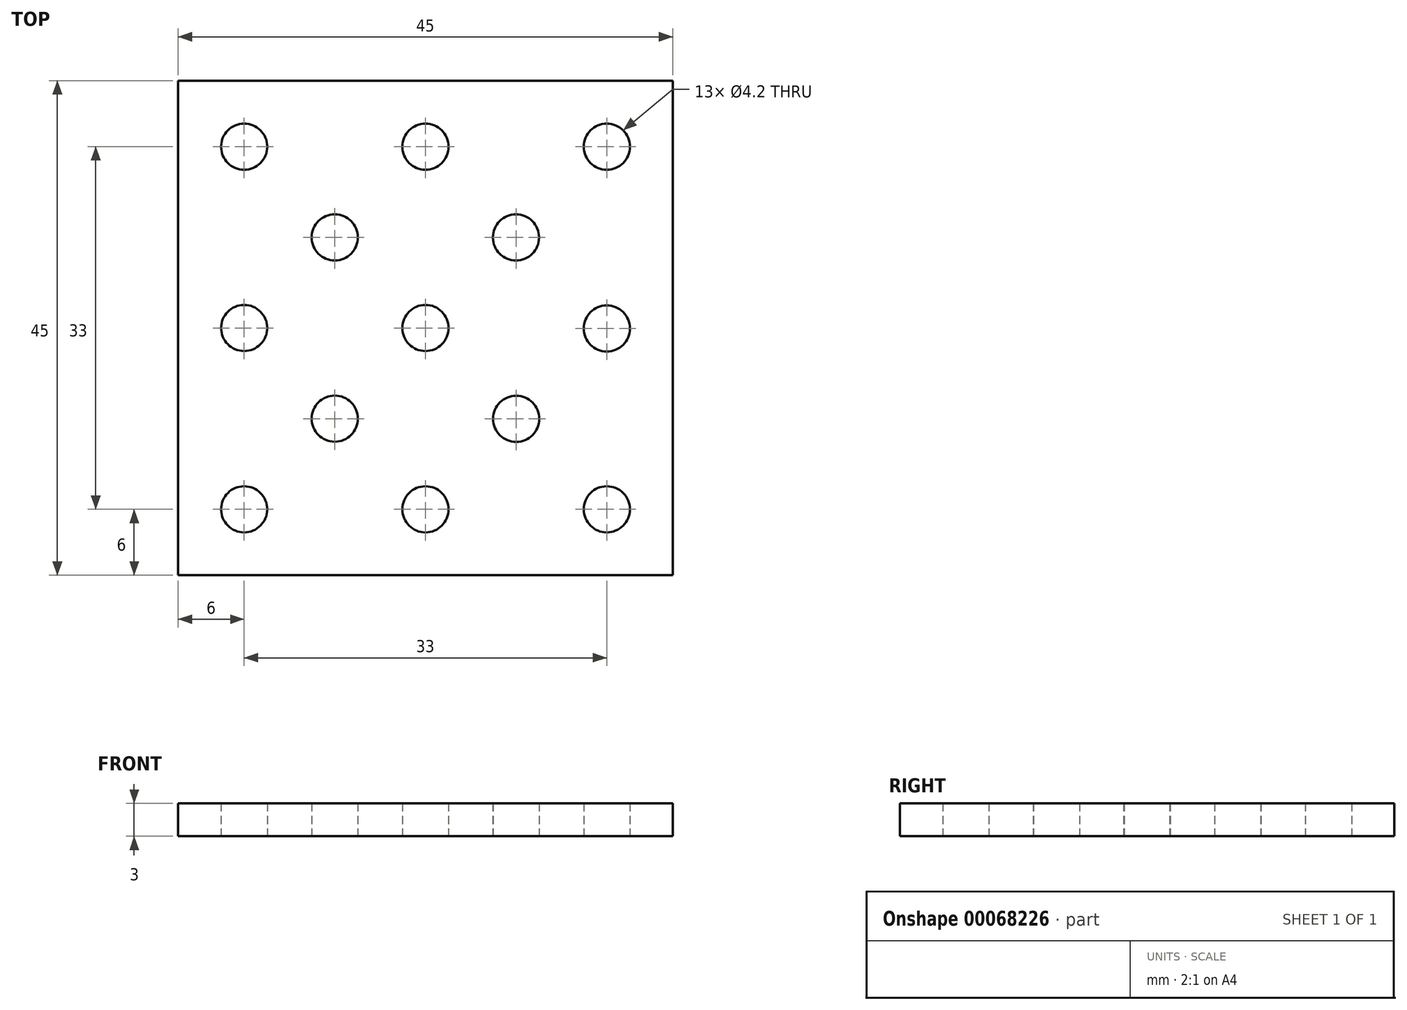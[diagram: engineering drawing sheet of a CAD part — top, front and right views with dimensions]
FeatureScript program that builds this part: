
annotation { "Feature Type Name" : "Feature", "Feature Type Description" : "" }
export const myFeature = defineFeature(function(context is Context, id is Id, definition is map)
    precondition{}
    {
        {
            var Q0;
            Q0=qCreatedBy(makeId("Top.planeOp"),FACE);
            var sketch = newSketch(context, id + "F0", { "sketchPlane" : qUnion([Q0])});
            skLineSegment(sketch, "E0.rect.bottom", {"start": v(-22.5, 22.5) * mm, "end": v(22.5, 22.5) * mm});
            skLineSegment(sketch, "E0.rect.top", {"start": v(-22.5, -22.5) * mm, "end": v(22.5, -22.5) * mm});
            skLineSegment(sketch, "E0.rect.left", {"start": v(-22.5, 22.5) * mm, "end": v(-22.5, -22.5) * mm});
            skLineSegment(sketch, "E0.rect.right", {"start": v(22.5, 22.5) * mm, "end": v(22.5, -22.5) * mm});
            skPoint(sketch, "E0.rect.middle", {"position": v(0, 0) * mm});
            skCircle(sketch, "E1", {"center": v(-16.5, 16.5) * mm, "radius": 2.1 * mm});
            skCircle(sketch, "E2.MirrorC", {"center": v(16.5, 16.5) * mm, "radius": 2.1 * mm});
            skCircle(sketch, "E3.MirrorC", {"center": v(16.5, -16.5) * mm, "radius": 2.1 * mm});
            skCircle(sketch, "E4.MirrorC", {"center": v(-16.5, -16.5) * mm, "radius": 2.1 * mm});
            skCircle(sketch, "E5.MirrorC", {"center": v(16.5, -0.05) * mm, "radius": 2.1 * mm});
            skLineSegment(sketch, "E6", {"start": v(16.5, 16.5) * mm, "end": v(16.5, -16.5) * mm, "construction": true});
            skLineSegment(sketch, "E7", {"start": v(16.5, -16.5) * mm, "end": v(-16.5, -16.5) * mm, "construction": true});
            skLineSegment(sketch, "E8", {"start": v(-16.5, -16.5) * mm, "end": v(-16.5, 16.5) * mm, "construction": true});
            skLineSegment(sketch, "E9", {"start": v(-16.5, 16.5) * mm, "end": v(16.5, 16.5) * mm, "construction": true});
            skCircle(sketch, "E10.MirrorC", {"center": v(0, -16.5) * mm, "radius": 2.1 * mm});
            skLineSegment(sketch, "E11", {"start": v(-16.5, 0) * mm, "end": v(0, -16.5) * mm, "construction": true});
            skLineSegment(sketch, "E12", {"start": v(16.5, -0.05) * mm, "end": v(0, -16.5) * mm, "construction": true});
            skLineSegment(sketch, "E13", {"start": v(16.5, -0.05) * mm, "end": v(0, 16.5) * mm, "construction": true});
            skLineSegment(sketch, "E14", {"start": v(-16.5, -16.5) * mm, "end": v(16.5, 16.5) * mm, "construction": true});
            skPoint(sketch, "E15", {"position": v(8.24, 8.24) * mm});
            skPoint(sketch, "E16", {"position": v(-8.25, -8.25) * mm});
            skCircle(sketch, "E17.MirrorC", {"center": v(-8.25, -8.25) * mm, "radius": 2.1 * mm});
            skCircle(sketch, "E18.MirrorC", {"center": v(8.24, 8.24) * mm, "radius": 2.1 * mm});
            skLineSegment(sketch, "E19", {"start": v(-16.5, 16.5) * mm, "end": v(16.5, -16.5) * mm, "construction": true});
            skPoint(sketch, "E20", {"position": v(8.26, -8.26) * mm});
            skCircle(sketch, "E21.MirrorC", {"center": v(8.26, -8.26) * mm, "radius": 2.1 * mm});
            skLineSegment(sketch, "E22.bottom", {"start": v(-22.5, 22.5) * mm, "end": v(7.5, 22.5) * mm, "construction": true});
            skLineSegment(sketch, "E22.top", {"start": v(-22.5, -7.5) * mm, "end": v(7.5, -7.5) * mm, "construction": true});
            skLineSegment(sketch, "E22.left", {"start": v(-22.5, 22.5) * mm, "end": v(-22.5, -7.5) * mm, "construction": true});
            skLineSegment(sketch, "E22.right", {"start": v(7.5, 22.5) * mm, "end": v(7.5, -7.5) * mm, "construction": true});
            skCircle(sketch, "E23.MirrorC", {"center": v(0, 0) * mm, "radius": 2.1 * mm});
            skPoint(sketch, "E24", {"position": v(-16.5, 0) * mm});
            skCircle(sketch, "E25.MirrorC", {"center": v(-16.5, 0) * mm, "radius": 2.1 * mm});
            skLineSegment(sketch, "E26", {"start": v(-16.5, 0) * mm, "end": v(0, 16.5) * mm, "construction": true});
            skPoint(sketch, "E27", {"position": v(-8.25, 8.25) * mm});
            skCircle(sketch, "E28", {"center": v(-8.25, 8.25) * mm, "radius": 2.1 * mm});
            skCircle(sketch, "E29", {"center": v(0, 16.5) * mm, "radius": 2.1 * mm});
            skSolve(sketch);
        }
        {
            var Q0;
            Q0 = qSketchRegion(id + "F0", true);
            extrude(context, id + "F1", {"entities" : qUnion([Q0]), "depth" : 3 * mm});
        }
    });
